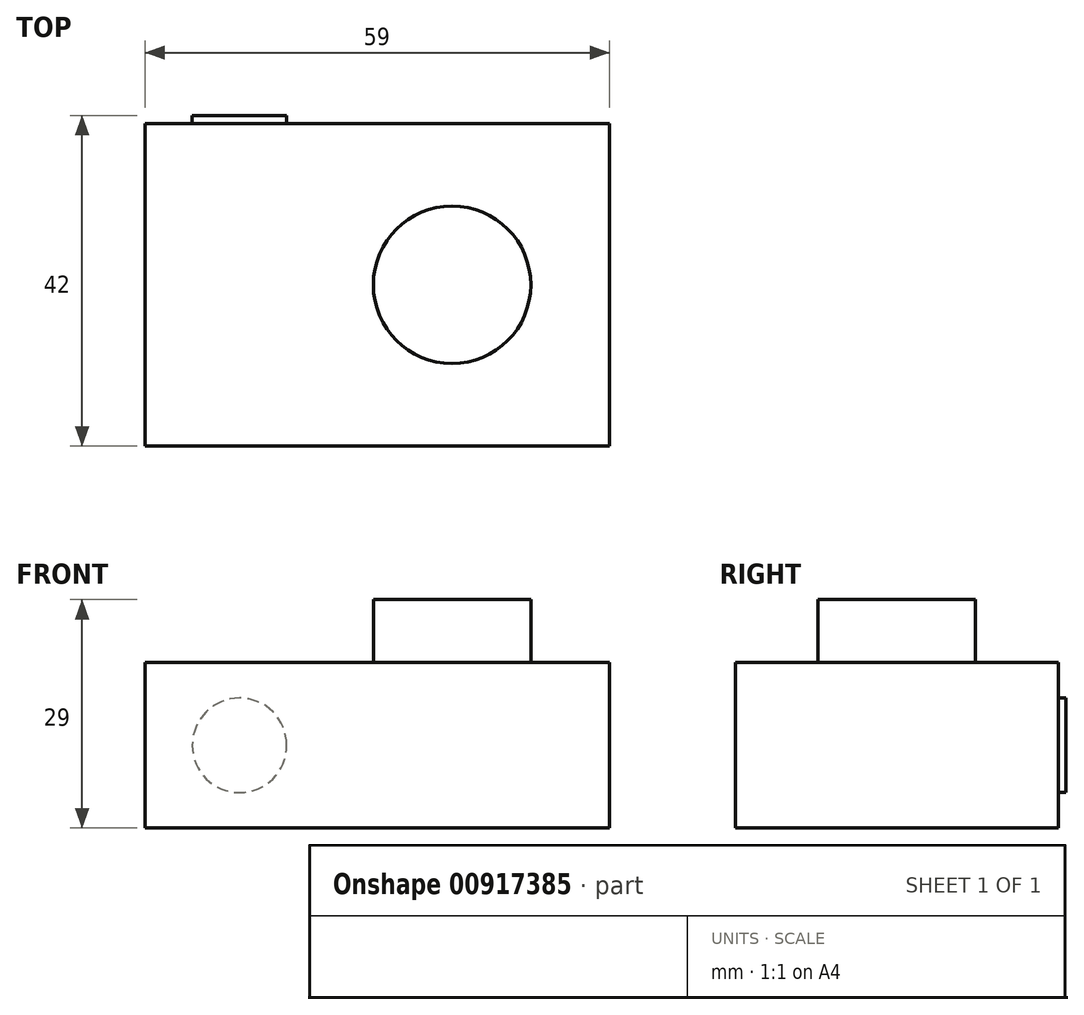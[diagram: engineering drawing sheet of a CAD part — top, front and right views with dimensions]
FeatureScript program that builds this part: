
annotation { "Feature Type Name" : "Feature", "Feature Type Description" : "" }
export const myFeature = defineFeature(function(context is Context, id is Id, definition is map)
    precondition{}
    {
        {
            var Q0;
            Q0=qCreatedBy(makeId("Top.planeOp"),FACE);
            var sketch = newSketch(context, id + "F0", { "sketchPlane" : qUnion([Q0])});
            skLineSegment(sketch, "E0.bottom", {"start": v(-29.5, 20.5) * mm, "end": v(29.5, 20.5) * mm});
            skLineSegment(sketch, "E0.top", {"start": v(-29.5, -20.5) * mm, "end": v(29.5, -20.5) * mm});
            skLineSegment(sketch, "E0.left", {"start": v(-29.5, 20.5) * mm, "end": v(-29.5, -20.5) * mm});
            skLineSegment(sketch, "E0.right", {"start": v(29.5, 20.5) * mm, "end": v(29.5, -20.5) * mm});
            skPoint(sketch, "E0.middle", {"position": v(0, 0) * mm});
            skSolve(sketch);
        }
        {
            var Q0;
            Q0 = qSketchRegion(id + "F0", true);
            extrude(context, id + "F1", {"entities" : qUnion([Q0]), "depth" : 21 * mm, "offsetDistance" : 25 * mm});
        }
        {
            var Q0;
            Q0=makeQuery(id+"F1.opExtrude","CAP_FACE",FACE,{"disambiguationData":[OSD([sQuery(id+"F0.wireOp",EDGE,"E0.bottom"),sQuery(id+"F0.wireOp",EDGE,"E0.top"),sQuery(id+"F0.wireOp",EDGE,"E0.left"),sQuery(id+"F0.wireOp",EDGE,"E0.right")])],"isStart":false});
            var sketch = newSketch(context, id + "F2", { "sketchPlane" : qUnion([Q0])});
            skCircle(sketch, "E1", {"center": v(9.5, 0) * mm, "radius": 10 * mm});
            skSolve(sketch);
        }
        {
            var Q0;
            Q0 = qSketchRegion(id + "F2", true);
            extrude(context, id + "F3", {"entities" : qUnion([Q0]), "operationType" : NewBodyOperationType.ADD, "depth" : 8 * mm, "offsetDistance" : 25 * mm});
        }
        {
            var Q0;
            Q0=makeQuery(id+"F1.opExtrude","SWEPT_FACE",FACE,{"disambiguationData":[OSD([sQuery(id+"F0.wireOp",EDGE,"E0.bottom")])]});
            var sketch = newSketch(context, id + "F4", { "sketchPlane" : qUnion([Q0])});
            skCircle(sketch, "E2", {"center": v(17.5, 10.5) * mm, "radius": 6 * mm});
            skSolve(sketch);
        }
        {
            var Q0;
            Q0 = qSketchRegion(id + "F4", true);
            extrude(context, id + "F5", {"entities" : qUnion([Q0]), "operationType" : NewBodyOperationType.ADD, "depth" : 1 * mm, "offsetDistance" : 25 * mm});
        }
    });
